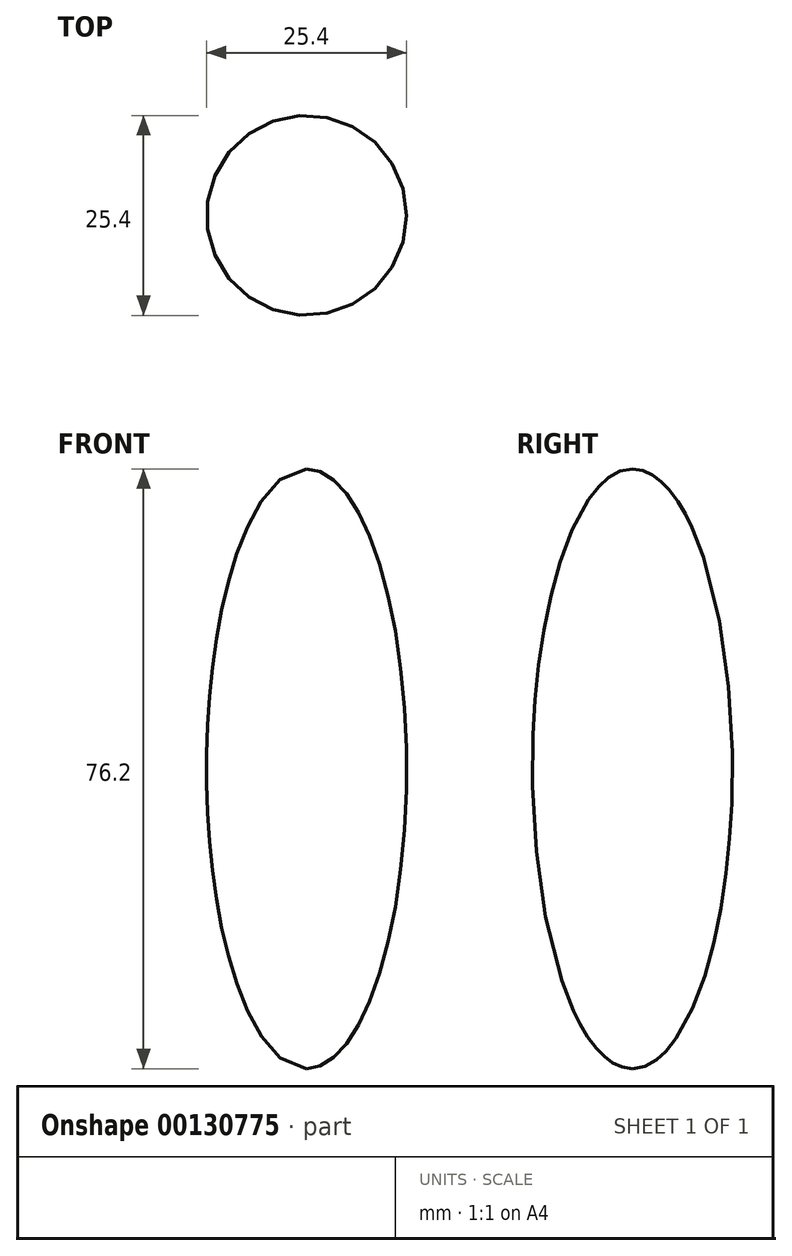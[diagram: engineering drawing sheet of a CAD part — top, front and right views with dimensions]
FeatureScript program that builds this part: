
annotation { "Feature Type Name" : "Feature", "Feature Type Description" : "" }
export const myFeature = defineFeature(function(context is Context, id is Id, definition is map)
    precondition{}
    {
        {
            var Q0;
            Q0=qCreatedBy(makeId("Front.planeOp"),FACE);
            var sketch = newSketch(context, id + "F0", { "sketchPlane" : qUnion([Q0])});
            skEllipticalArc(sketch, "E0", {});
            skLineSegment(sketch, "E1", {"start": v(0, 0) * mm, "end": v(0, 38.1) * mm});
            skLineSegment(sketch, "E2", {"start": v(0, 0) * mm, "end": v(12.7, 0) * mm});
            skLineSegment(sketch, "E3", {"start": v(0, 0) * mm, "end": v(0, -38.1) * mm});
            const initialGuessF0  = {"E0": [0, 0, 0, 1, 0.0381, 0.0127, 3.141592653589793, 0]};
            skSetInitialGuess(sketch, initialGuessF0);
            skSolve(sketch);
        }
        {
            var Q0;
            Q0 = qSketchRegion(id + "F0", true);
            var Q1;
            Q1=sQuery(id+"F0.wireOp",EDGE,"E1");
            revolve(context, id + "F1", {"entities" : qUnion([Q0]), "axis" : qUnion([Q1]), "revolveType" : RevolveType.FULL});
        }
    });
